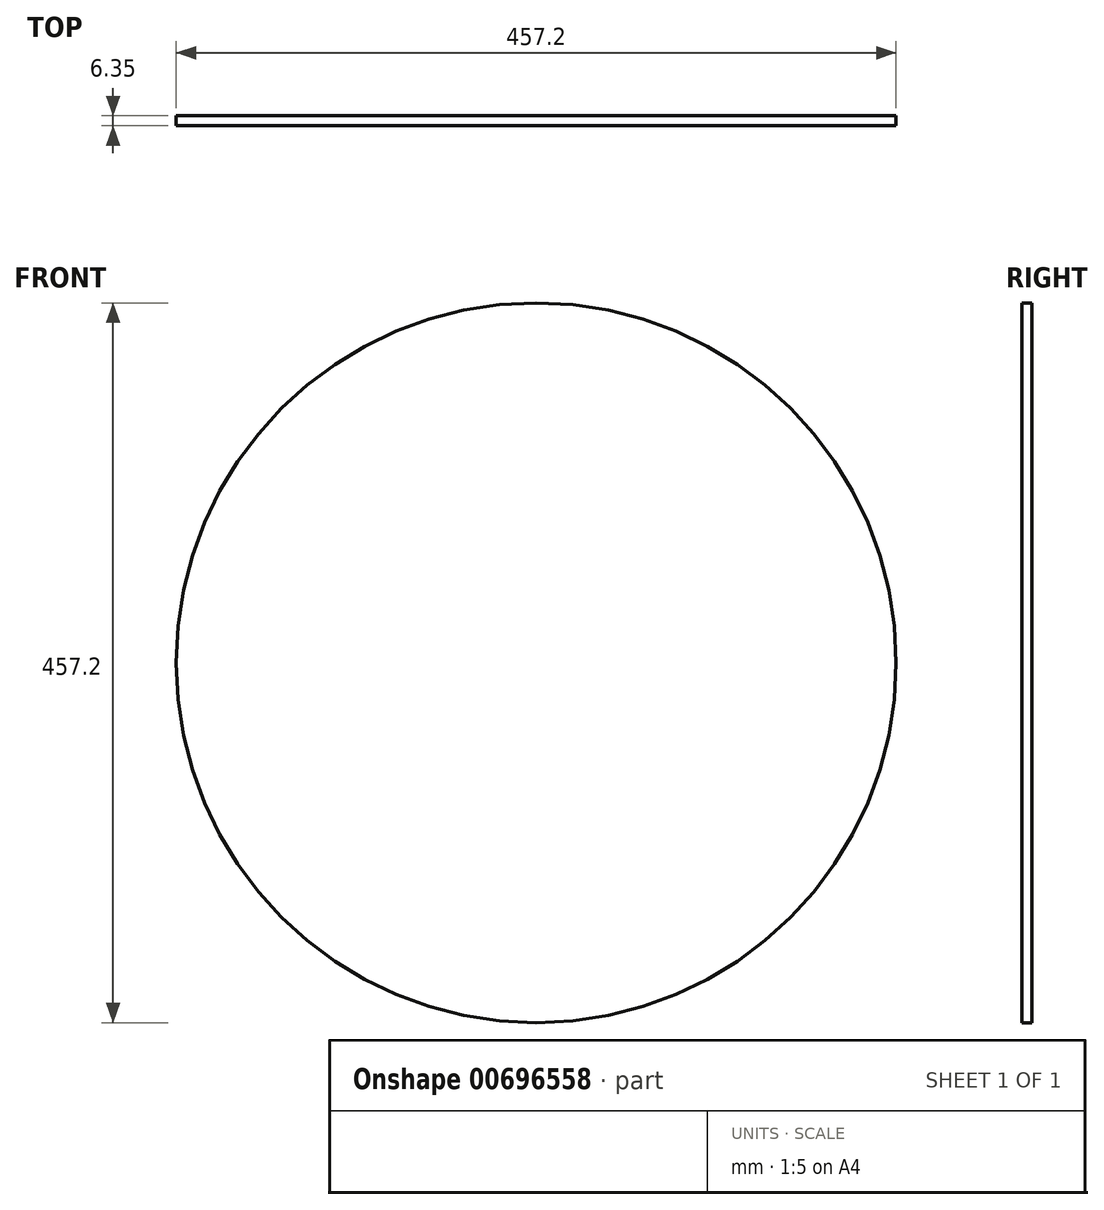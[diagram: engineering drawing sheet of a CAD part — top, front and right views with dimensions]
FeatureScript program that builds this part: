
annotation { "Feature Type Name" : "Feature", "Feature Type Description" : "" }
export const myFeature = defineFeature(function(context is Context, id is Id, definition is map)
    precondition{}
    {
        {
            var Q0;
            Q0=qCreatedBy(makeId("Front.planeOp"),FACE);
            var sketch = newSketch(context, id + "F0", { "sketchPlane" : qUnion([Q0])});
            skCircle(sketch, "E0", {"center": v(0, 0) * mm, "radius": 228.6 * mm});
            skSolve(sketch);
        }
        {
            var Q0;
            Q0=makeQuery(id+"F0.imprint","IMPRINT",FACE,{"disambiguationData":[TD([[makeQuery(id+"F0.imprint","IMPRINT",EDGE,{"derivedFrom":sQuery(id+"F0.wireOp",EDGE,"E0")}),1.0]])]});
            extrude(context, id + "F1", {"entities" : qUnion([Q0]), "depth" : 6.35 * mm, "offsetDistance" : 25.4 * mm});
        }
    });
